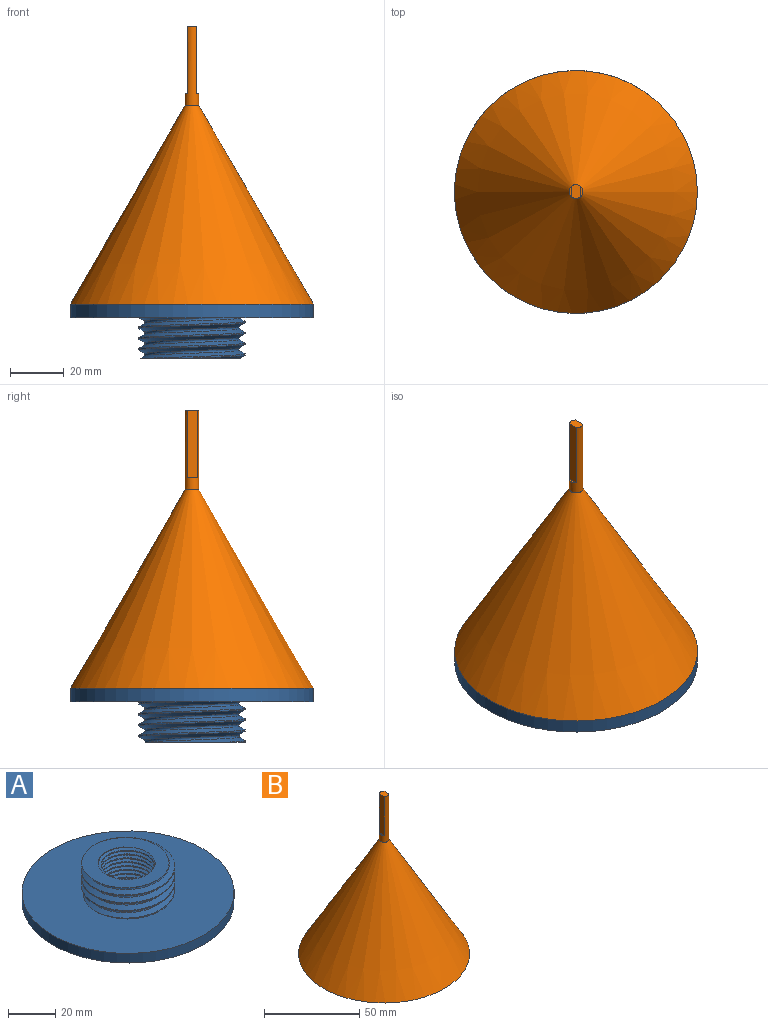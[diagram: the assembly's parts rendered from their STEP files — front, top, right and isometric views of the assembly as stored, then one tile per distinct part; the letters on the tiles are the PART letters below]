
ASSEMBLY  parts=2 mates=1
PART A: 12 faces, bbox 91.3x91.3x24.1 mm
  f0: plane 90.6x90.6mm, normal (0,0,-1), area 5910.4mm2, adj f2,f8,f9,f10,f11
  f1: plane 38.45x38.24mm, normal (0,0,1), area 625.5mm2, adj f4,f5,f6,f7,f8,f9,f10,f11
  f2: cylinder r=45mm len=90mm, axis (0,0,-1), area 1413.7mm2, adj f0,f3
  f3: plane 91.13x91.13mm, normal (0,0,1), area 5284.7mm2, adj f2,f4,f5,f6,f7
  f4: cylinder r=19.75mm len=39.5mm, axis (0,0,-1), area 259.7mm2, adj f1,f3,f6,f7
  f5: bspline ~40.61x35.17mm, area 460.7mm2, adj f1,f3,f6,f7
  f6: bspline ~45.61x39.5mm, area 1099.1mm2, adj f1,f3,f4,f5
  f7: bspline ~45.61x39.5mm, area 1099.6mm2, adj f1,f3,f4,f5
  f8: bspline ~29.06x25.17mm, area 196mm2, adj f0,f1,f10,f11
  f9: bspline ~29.06x25.17mm, area 946.5mm2, adj f0,f1,f10,f11
  f10: bspline ~29.27x25.35mm, area 229.9mm2, adj f0,f1,f8,f9
  f11: cylinder r=11.5mm len=23mm, axis (0,0,-1), area 391.4mm2, adj f0,f1,f8,f9
PART B: 9 faces, bbox 90x90x103 mm
  f0: plane 5.1x3.5mm, normal (0,0,1), area 16.3mm2, adj f4,f5,f7
  f1: cone r=45mm half-angle=30deg, axis (0,0,-1), area 12682.6mm2, adj f2,f4
  f2: plane 90x90mm, normal (0,0,-1), area 1527.7mm2, adj f1,f3
  f3: cone r=40.67mm half-angle=30deg, axis (0,0,-1), area 9668.1mm2, adj f2
  f4: cylinder r=2.55mm len=29.47mm, axis (0,0,-1), area 264.6mm2, adj f0,f1,f5,f6,f7,f8
  f5: plane 25x3.71mm, normal (1,0,0), area 92.7mm2, adj f0,f4,f6
  f6: plane 3.71x0.8mm, normal (0,0,1), area 2.1mm2, adj f4,f5
  f7: plane 25x3.71mm, normal (-1,0,0), area 92.7mm2, adj f0,f4,f8
  f8: plane 3.71x0.8mm, normal (0,0,1), area 2.1mm2, adj f4,f7
PLACE A rot(axis=(1,0,0),180deg) t=(-48.69,-14.68,-68.39)mm
PLACE B t=(-48.68,-14.7,-68.39)mm
MATE planar A.f0 <-> B.f1  axis (0,0,1) through (-48.66,-14.65,-68.39)mm
